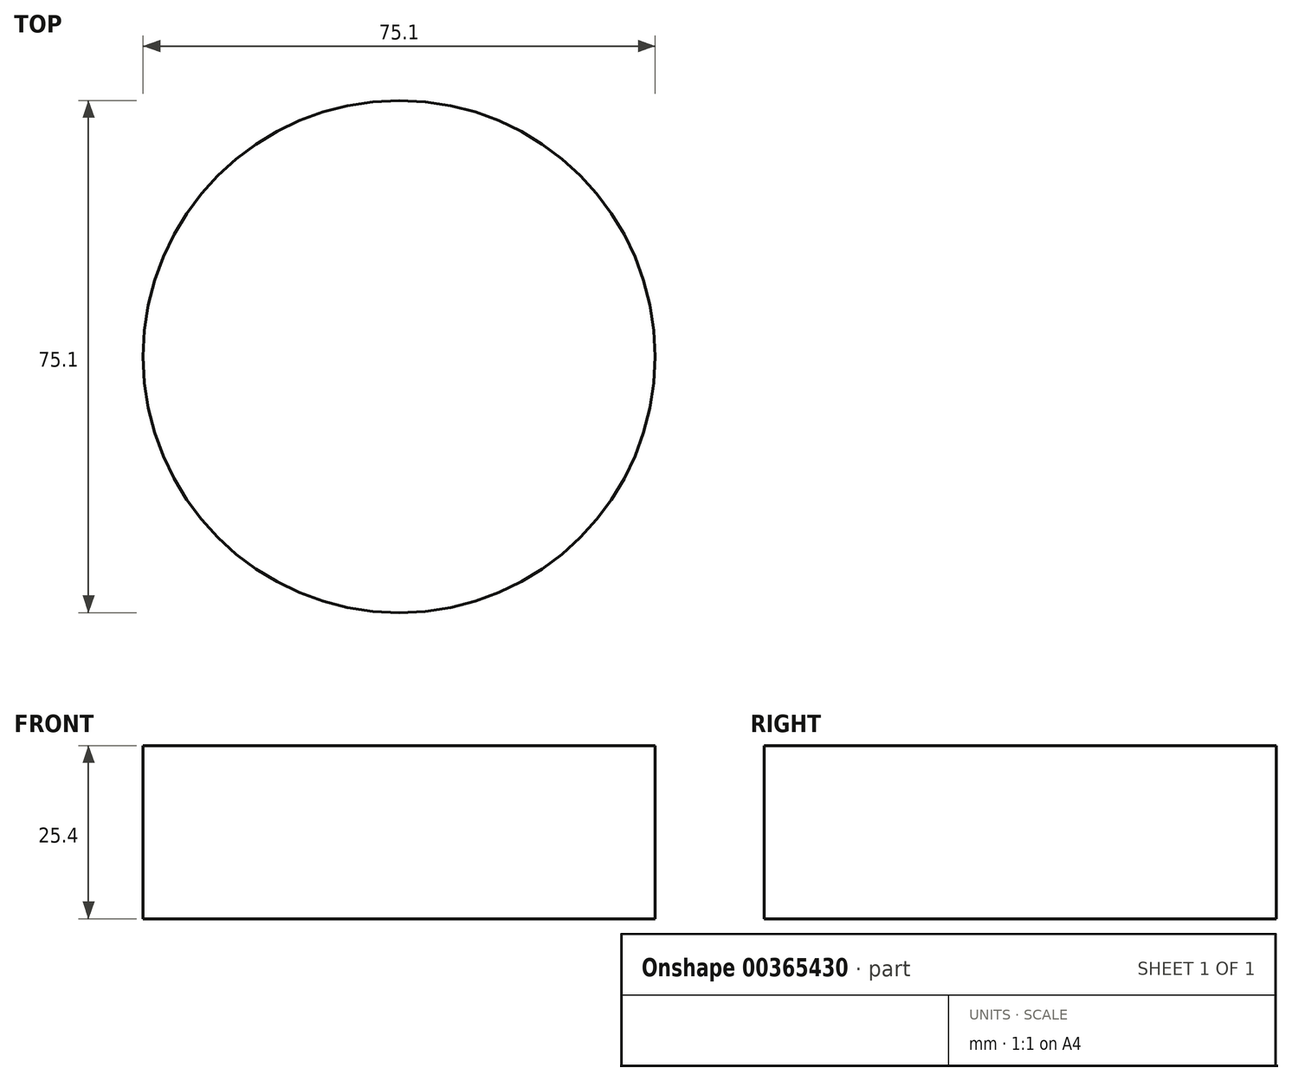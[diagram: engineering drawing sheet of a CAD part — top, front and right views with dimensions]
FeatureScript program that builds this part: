
annotation { "Feature Type Name" : "Feature", "Feature Type Description" : "" }
export const myFeature = defineFeature(function(context is Context, id is Id, definition is map)
    precondition{}
    {
        {
            var Q0;
            Q0=qCreatedBy(makeId("Top.planeOp"),FACE);
            var sketch = newSketch(context, id + "F0", { "sketchPlane" : qUnion([Q0])});
            skCircle(sketch, "E0", {"center": v(0, 0) * mm, "radius": 37.55 * mm});
            skSolve(sketch);
        }
        {
            var Q0;
            Q0 = qSketchRegion(id + "F0", true);
            extrude(context, id + "F1", {"entities" : qUnion([Q0]), "depth" : 25.4 * mm});
        }
    });
